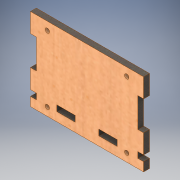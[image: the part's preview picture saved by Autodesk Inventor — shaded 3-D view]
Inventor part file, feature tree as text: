
AUTODESK INVENTOR PART (.ipt)
format: ipt  version: 2019 (Build 230136000, 136)  size: 176,128 bytes
history: native  units: mm
features: sketch x2, other x1, extrude x1, hole x1
ambient origin geometry x8: Origin, YZ Plane, XZ Plane, XY Plane, X Axis, Y Axis, Z Axis, Center Point
bodies: Body1 (feature_tree)
feature tree (5):
  other  "Твердое тело1"
  extrude  "Выдавливание1"  Depth=4.0mm
  hole  "Отверстие1"  [1 undecoded]
  sketch  "Эскиз1"
  sketch  "Эскиз2"
note: 1 required parameter value undecoded (feature->parameter linkage not recoverable at this tier; creation-order binding heuristic only, values carry confidence <= 0.55)
